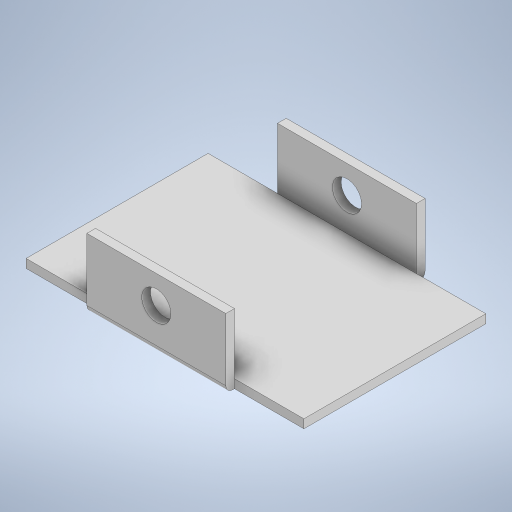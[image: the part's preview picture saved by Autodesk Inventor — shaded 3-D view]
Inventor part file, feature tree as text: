
AUTODESK INVENTOR PART (.ipt)
format: ipt  version: 2024 (Build 280153000, 153)  size: 261,120 bytes
history: native  units: in
note: dims shown in document units (in); Inventor stores cm internally (conversion verified against a paired STEP export)
features: extrude x4, sketch x4, fillet x1
ambient origin geometry x8: Origin, YZ Plane, XZ Plane, XY Plane, X Axis, Y Axis, Z Axis, Center Point
bodies: Solid1 (feature_tree)
feature tree (9):
  extrude  "Extrusion1"  Depth=1.31in
  extrude  "Extrusion2"  Depth=0.5in
  extrude  "Extrusion3"  Depth=0.5in
  extrude  "Extrusion4"  Depth=0.5in
  fillet  "Fillet1"  Radius=1.0in
  sketch  "Sketch1"  dims[d0=2.0in d1=1.31in]
  sketch  "Sketch2"  dims[d2=0.0625in d3=0.0in d4=0.5in]
  sketch  "Sketch3"  dims[d5=1.0in d6=0.5in]
  sketch  "Sketch4"  dims[d7=0.0625in d8=0.0in d9=0.5in d10=1.0in d11=0.5in d12=1.0in d13=0.0625in d14=0.0in d15=0.5in d16=0.2in d17=0.21in d18=2.0in d19=0.0in d20=0.05in]
